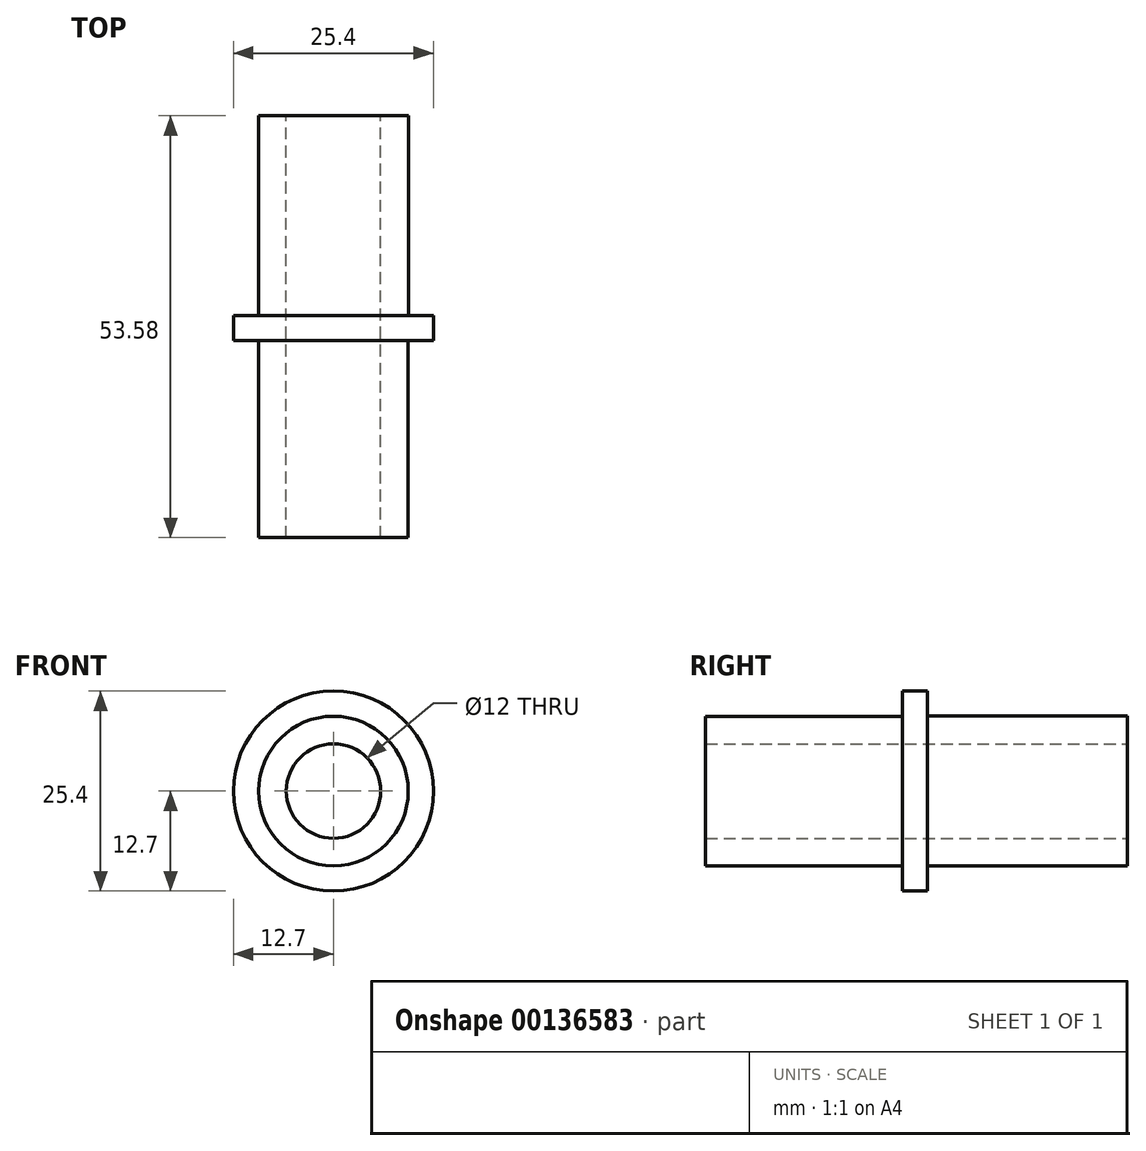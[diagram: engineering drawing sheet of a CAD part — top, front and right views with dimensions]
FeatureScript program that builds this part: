
annotation { "Feature Type Name" : "Feature", "Feature Type Description" : "" }
export const myFeature = defineFeature(function(context is Context, id is Id, definition is map)
    precondition{}
    {
        {
            var Q0;
            Q0=qCreatedBy(makeId("Front.planeOp"),FACE);
            var sketch = newSketch(context, id + "F0", { "sketchPlane" : qUnion([Q0])});
            skCircle(sketch, "E0", {"center": v(0, 0) * mm, "radius": 9.53 * mm});
            skCircle(sketch, "E1", {"center": v(0, 0) * mm, "radius": 6 * mm});
            skSolve(sketch);
        }
        {
            var Q0;
            Q0=makeQuery(id+"F0.imprint","IMPRINT",FACE,{"disambiguationData":[TD([[makeQuery(id+"F0.imprint","IMPRINT",EDGE,{"derivedFrom":sQuery(id+"F0.wireOp",EDGE,"E0")}),1.0]])]});
            extrude(context, id + "F1", {"entities" : qUnion([Q0]), "depth" : 25.4 * mm});
        }
        {
            var Q0;
            Q0=makeQuery(id+"F1.opExtrude","CAP_FACE",FACE,{"disambiguationData":[OSD([sQuery(id+"F0.wireOp",EDGE,"E0"),sQuery(id+"F0.wireOp",EDGE,"E1")])],"isStart":false});
            var sketch = newSketch(context, id + "F2", { "sketchPlane" : qUnion([Q0])});
            skCircle(sketch, "E2", {"center": v(0, 0) * mm, "radius": 12.7 * mm});
            skSolve(sketch);
        }
        {
            var Q0;
            Q0=makeQuery(id+"F2.imprint","IMPRINT",FACE,{"disambiguationData":[TD([[makeQuery(id+"F2.imprint","IMPRINT",EDGE,{"derivedFrom":sQuery(id+"F2.wireOp",EDGE,"E2")}),1.0]])]});
            var Q1;
            Q1=makeQuery(id+"F2.imprint","IMPRINT",FACE,{"disambiguationData":[TD([[makeQuery(id+"F2.imprint","IMPRINT",EDGE,{"derivedFrom":makeQuery(id+"F1.opExtrude","CAP_EDGE",EDGE,{"disambiguationData":[OSD([sQuery(id+"F0.wireOp",EDGE,"E0")])],"isStart":false})}),1.0]])]});
            extrude(context, id + "F3", {"entities" : qUnion([Q0, Q1]), "operationType" : NewBodyOperationType.ADD, "depth" : 3.17 * mm});
        }
        {
            var Q0;
            Q0=makeQuery(id+"F3.opExtrude","CAP_FACE",FACE,{"disambiguationData":[OSD([sQuery(id+"F0.wireOp",EDGE,"E1"),sQuery(id+"F2.wireOp",EDGE,"E2")])],"isStart":false});
            var sketch = newSketch(context, id + "F4", { "sketchPlane" : qUnion([Q0])});
            skCircle(sketch, "E3", {"center": v(0, 0) * mm, "radius": 9.5 * mm});
            skSolve(sketch);
        }
        {
            var Q0;
            Q0=makeQuery(id+"F4.imprint","IMPRINT",FACE,{"disambiguationData":[TD([[makeQuery(id+"F4.imprint","IMPRINT",EDGE,{"derivedFrom":sQuery(id+"F4.wireOp",EDGE,"E3")}),1.0]])]});
            extrude(context, id + "F5", {"entities" : qUnion([Q0]), "operationType" : NewBodyOperationType.ADD, "depth" : 25 * mm});
        }
    });
